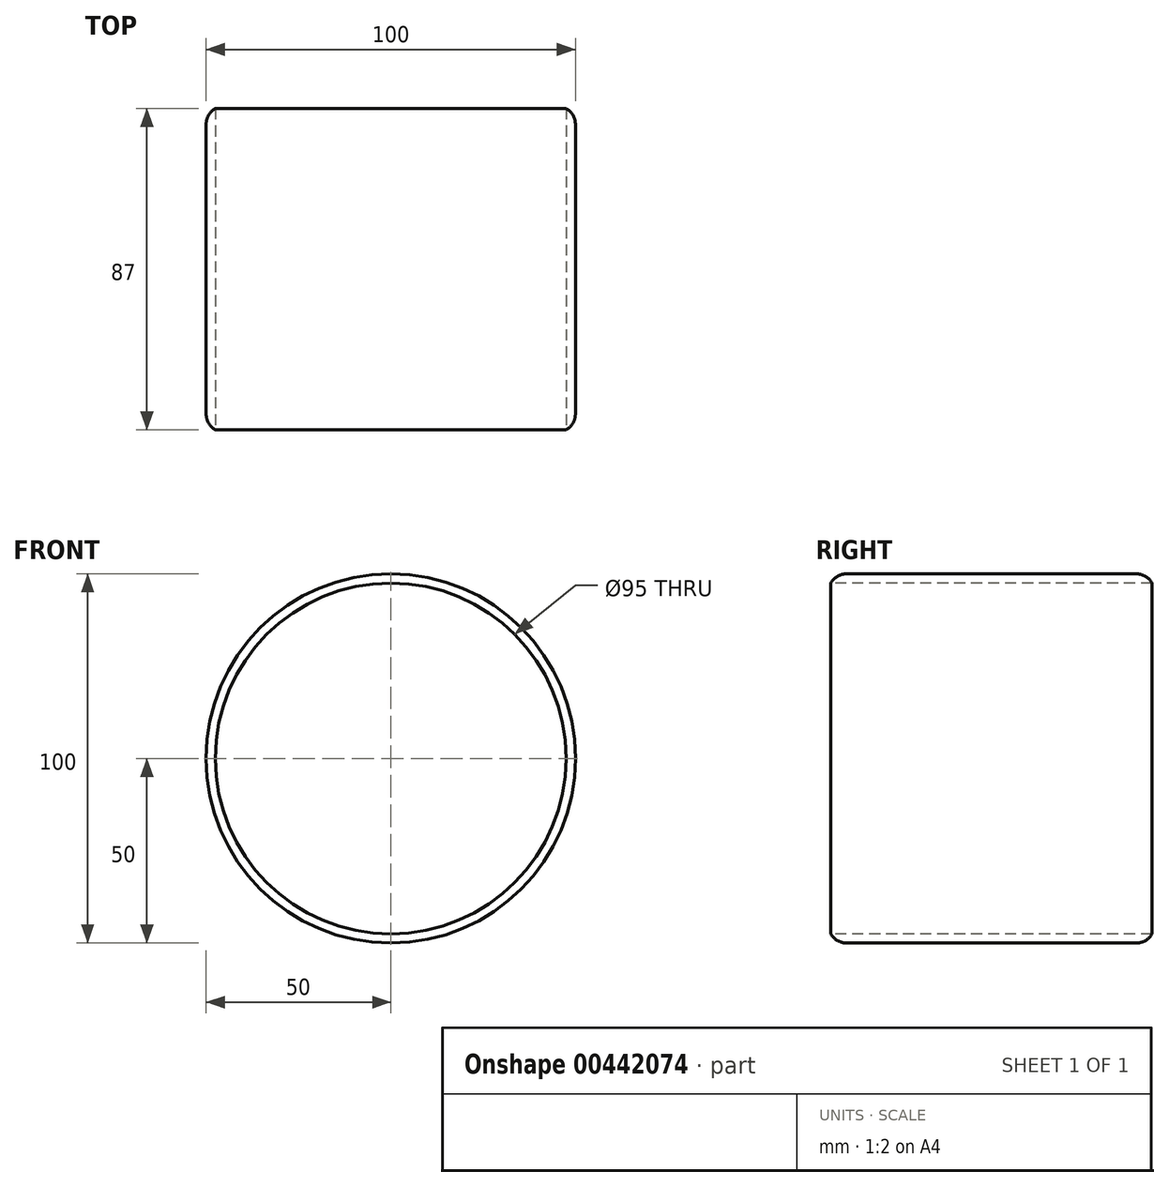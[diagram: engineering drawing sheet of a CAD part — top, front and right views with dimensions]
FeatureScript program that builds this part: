
annotation { "Feature Type Name" : "Feature", "Feature Type Description" : "" }
export const myFeature = defineFeature(function(context is Context, id is Id, definition is map)
    precondition{}
    {
        {
            var Q0;
            Q0=qCreatedBy(makeId("Front.planeOp"),FACE);
            var sketch = newSketch(context, id + "F0", { "sketchPlane" : qUnion([Q0])});
            skCircle(sketch, "E0", {"center": v(0, 0) * mm, "radius": 50 * mm});
            skSolve(sketch);
        }
        {
            var Q0;
            Q0=makeQuery(id+"F0.imprint","IMPRINT",FACE,{"disambiguationData":[TD([[makeQuery(id+"F0.imprint","IMPRINT",EDGE,{"derivedFrom":sQuery(id+"F0.wireOp",EDGE,"E0")}),1.0]])]});
            extrude(context, id + "F1", {"entities" : qUnion([Q0]), "oppositeDirection" : true, "depth" : 87 * mm});
        }
        {
            var Q0;
            Q0=makeQuery(id+"F1.opExtrude","CAP_FACE",FACE,{"disambiguationData":[OSD([sQuery(id+"F0.wireOp",EDGE,"E0")])],"isStart":true});
            var sketch = newSketch(context, id + "F2", { "sketchPlane" : qUnion([Q0])});
            skCircle(sketch, "E1", {"center": v(0, 0) * mm, "radius": 47.5 * mm});
            skSolve(sketch);
        }
        {
            var Q0;
            Q0=sQuery(id+"F2.wireOp",VERTEX,"E1.center");
            var Q1;
            Q1=makeQuery(id+"F1.opExtrude","SWEPT_BODY",BODY,{"disambiguationData":[OSD([sQuery(id+"F0.wireOp",EDGE,"E0")])]});
            hole(context, id + "F3", {"style" : HoleStyle.SIMPLE, "endStyle" : HoleEndStyle.BLIND, "holeDiameter" : 95 * mm, "holeDepth" : 100 * mm, "isTappedThrough" : true, "tappedDepth" : 12 * mm, "tapClearance" : 3, "startFromSketch" : true, "locations" : qUnion([Q0]), "scope" : qUnion([Q1])});
        }
        {
            var Q0;
            Q0=makeQuery(id+"F1.opExtrude","CAP_EDGE",EDGE,{"disambiguationData":[OSD([sQuery(id+"F0.wireOp",EDGE,"E0")])],"isStart":true});
            var Q1;
            Q1=makeQuery(id+"F1.opExtrude","CAP_EDGE",EDGE,{"disambiguationData":[OSD([sQuery(id+"F0.wireOp",EDGE,"E0")])],"isStart":false});
            fillet(context, id + "F4", {"entities" : qUnion([Q0, Q1]), "radius" : 5 * mm, "tangentPropagation" : true, "allowEdgeOverflow" : false});
        }
    });
